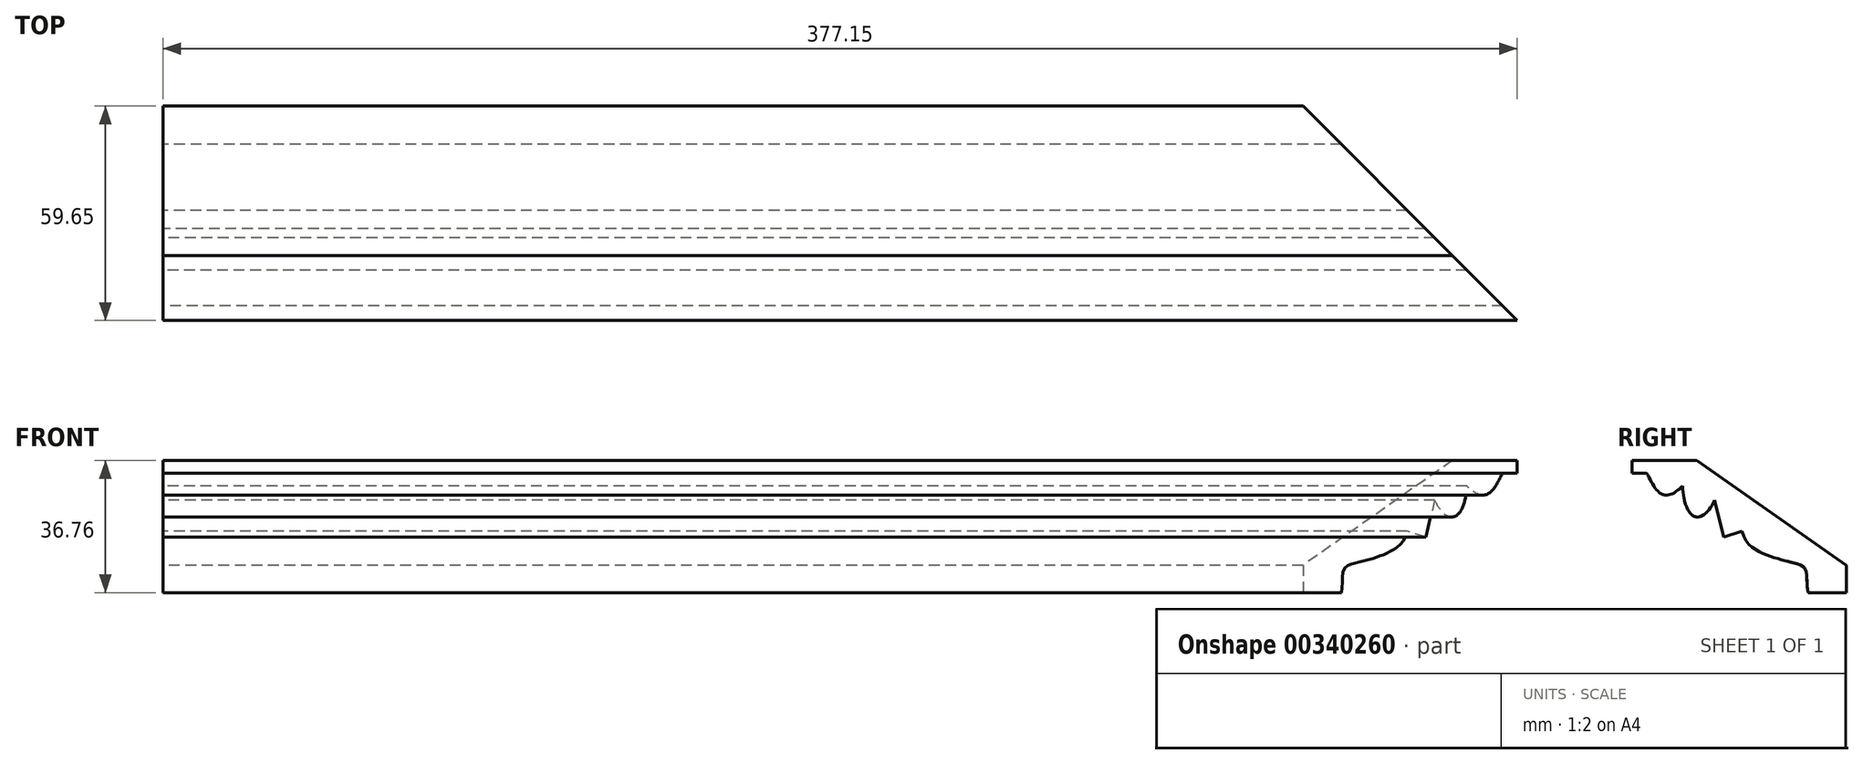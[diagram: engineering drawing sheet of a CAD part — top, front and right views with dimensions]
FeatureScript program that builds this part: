
annotation { "Feature Type Name" : "Feature", "Feature Type Description" : "" }
export const myFeature = defineFeature(function(context is Context, id is Id, definition is map)
    precondition{}
    {
        {
            var Q0;
            Q0=qCreatedBy(makeId("Right.planeOp"),FACE);
            var sketch = newSketch(context, id + "F0", { "sketchPlane" : qUnion([Q0])});
            skLineSegment(sketch, "E0", {"start": v(0, 7.62) * mm, "end": v(-41.61, 36.76) * mm});
            skLineSegment(sketch, "E1", {"start": v(-41.61, 36.76) * mm, "end": v(-59.65, 36.76) * mm});
            skLineSegment(sketch, "E2", {"start": v(-59.65, 36.76) * mm, "end": v(-59.65, 33.27) * mm});
            skLineSegment(sketch, "E3", {"start": v(-59.65, 33.27) * mm, "end": v(-55.58, 33.27) * mm});
            skLineSegment(sketch, "E4", {"start": v(0, 7.62) * mm, "end": v(0, 0) * mm});
            skLineSegment(sketch, "E5", {"start": v(0, 0) * mm, "end": v(-10.67, 0) * mm});
            skFitSpline(sketch, "E6", {"points": [v(-10.67, 0) * mm, v(-11.13, 5.86) * mm, v(-13.39, 7.89) * mm, v(-29.01, 17.09) * mm], "startDerivative": vector(-5.08, 29.03) * mm, "endDerivative": vector(-6.54, 39.72) * mm});
            skLineSegment(sketch, "E7", {"start": v(-29.01, 17.09) * mm, "end": v(-34.16, 15.48) * mm});
            skLineSegment(sketch, "E8", {"start": v(-34.16, 15.48) * mm, "end": v(-36.66, 25.7) * mm});
            skFitSpline(sketch, "E9", {"points": [v(-45.63, 29.67) * mm, v(-52.53, 28.3) * mm, v(-55.58, 33.27) * mm], "startDerivative": vector(-24.15, -24.15) * mm, "endDerivative": vector(-16.65, 31.11) * mm});
            skFitSpline(sketch, "E10", {"points": [v(-45.63, 29.67) * mm, v(-36.66, 25.7) * mm], "startDerivative": vector(2.07, -32.09) * mm, "endDerivative": vector(9.32, 20.18) * mm});
            skSolve(sketch);
        }
        {
            var Q0;
            Q0=qSketchRegion(id+"F0",true);
            var Q1;
            Q1 = qSketchRegion(id + "F2", true);
            extrude(context, id + "F1", {"entities" : qUnion([Q0, Q1]), "depth" : 177.8 * mm, "hasSecondDirection" : true, "secondDirectionOppositeDirection" : true, "secondDirectionDepth" : 228.6 * mm});
        }
        {
            var Q0;
            Q0=qCreatedBy(makeId("Top.planeOp"),FACE);
            var sketch = newSketch(context, id + "F2", { "sketchPlane" : qUnion([Q0])});
            skLineSegment(sketch, "E11", {"start": v(-88.9, 0) * mm, "end": v(88.9, 0) * mm, "construction": true});
            skLineSegment(sketch, "E12", {"start": v(88.9, 0) * mm, "end": v(184.11, 0) * mm});
            skLineSegment(sketch, "E13", {"start": v(184.11, 0) * mm, "end": v(184.11, -95.21) * mm});
            skLineSegment(sketch, "E14", {"start": v(184.11, -95.21) * mm, "end": v(88.9, 0) * mm});
            skLineSegment(sketch, "E15", {"start": v(0, 0) * mm, "end": v(0, -141.75) * mm, "construction": true});
            skSolve(sketch);
        }
        {
            var Q0;
            Q0 = qSketchRegion(id + "F2", true);
            extrude(context, id + "F3", {"entities" : qUnion([Q0]), "operationType" : NewBodyOperationType.REMOVE, "endBound" : BoundingType.THROUGH_ALL, "depth" : 25.4 * mm});
        }
    });
